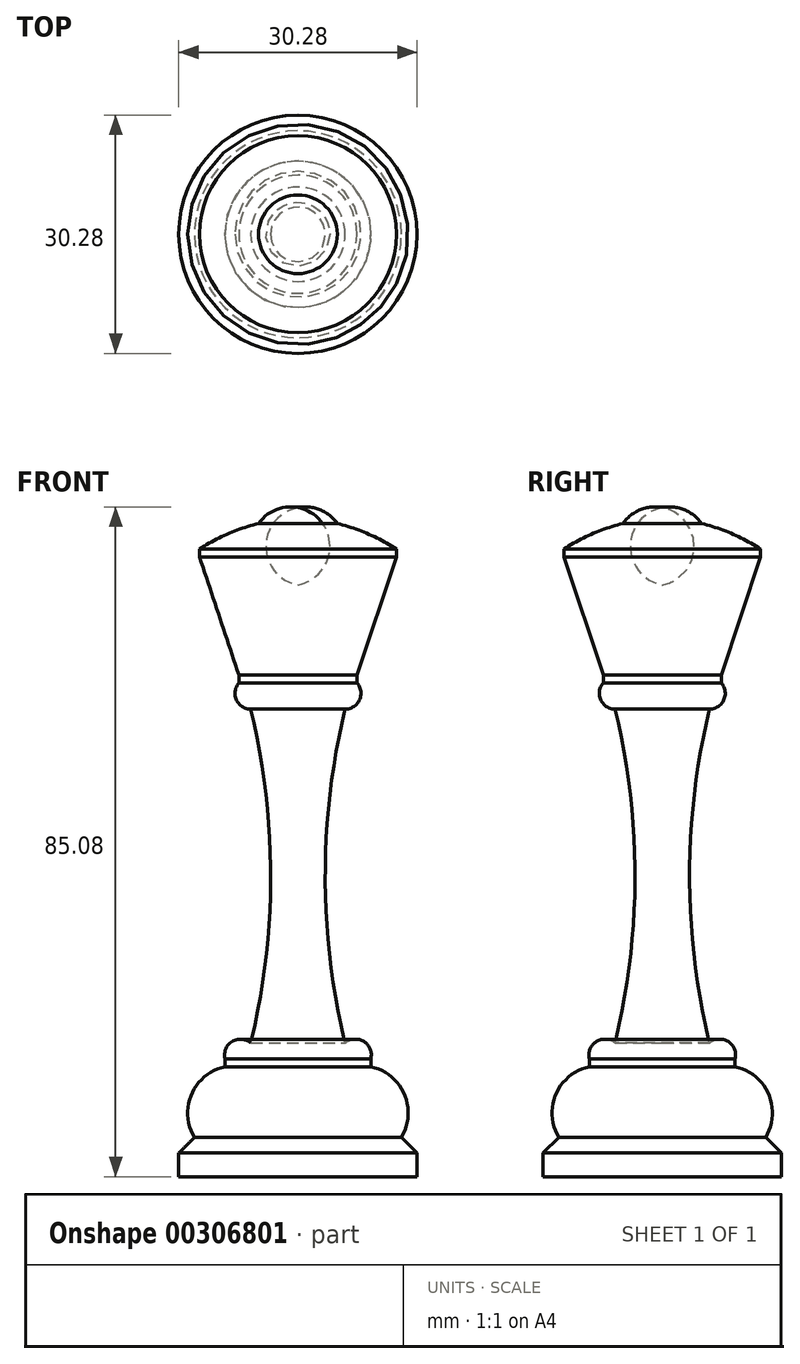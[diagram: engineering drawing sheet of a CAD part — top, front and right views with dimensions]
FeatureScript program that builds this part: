
annotation { "Feature Type Name" : "Feature", "Feature Type Description" : "" }
export const myFeature = defineFeature(function(context is Context, id is Id, definition is map)
    precondition{}
    {
        {
            var Q0;
            Q0=qCreatedBy(makeId("Front.planeOp"),FACE);
            var sketch = newSketch(context, id + "F0", { "sketchPlane" : qUnion([Q0])});
            skArc(sketch, "E0", {"start": v(5, -2) * mm, "mid": v(2.8, -0.27) * mm, "end": v(0, 0) * mm});
            skArc(sketch, "E1", {"start": v(12.5, -5.27) * mm, "mid": v(8.88, -3.33) * mm, "end": v(5, -2) * mm});
            skLineSegment(sketch, "E2", {"start": v(12.5, -5.27) * mm, "end": v(12.5, -6.27) * mm});
            skLineSegment(sketch, "E3", {"start": v(12.5, -6.27) * mm, "end": v(7.5, -21.27) * mm});
            skLineSegment(sketch, "E4", {"start": v(7.5, -21.27) * mm, "end": v(7.5, -22.27) * mm});
            skArc(sketch, "E5", {"start": v(6, -25.6) * mm, "mid": v(7.82, -24.41) * mm, "end": v(7.5, -22.27) * mm});
            skArc(sketch, "E6", {"start": v(6, -25.6) * mm, "mid": v(3.46, -46.8) * mm, "end": v(6, -68.02) * mm});
            skArc(sketch, "E7", {"start": v(9.26, -70.02) * mm, "mid": v(8.37, -67.82) * mm, "end": v(6, -68.02) * mm});
            skLineSegment(sketch, "E8", {"start": v(9.26, -70.02) * mm, "end": v(9.26, -71.02) * mm});
            skArc(sketch, "E9", {"start": v(13.14, -80) * mm, "mid": v(13.5, -74.5) * mm, "end": v(9.26, -71.02) * mm});
            skLineSegment(sketch, "E10", {"start": v(15.14, -82) * mm, "end": v(13.14, -80) * mm});
            skLineSegment(sketch, "E11", {"start": v(15.14, -85) * mm, "end": v(15.14, -82) * mm});
            skLineSegment(sketch, "E12", {"start": v(15.14, -85) * mm, "end": v(0, -85) * mm});
            skLineSegment(sketch, "E13", {"start": v(0, -85) * mm, "end": v(0, 0) * mm});
            skSolve(sketch);
        }
        {
            var Q0;
            Q0=makeQuery(id+"F0.imprint","IMPRINT",FACE,{"disambiguationData":[TD([[makeQuery(id+"F0.imprint","IMPRINT",EDGE,{"derivedFrom":sQuery(id+"F0.wireOp",EDGE,"E0")}),1.0]])]});
            var Q1;
            Q1=sQuery(id+"F0.wireOp",EDGE,"E13");
            revolve(context, id + "F1", {"entities" : qUnion([Q0]), "axis" : qUnion([Q1]), "revolveType" : RevolveType.FULL});
        }
    });
